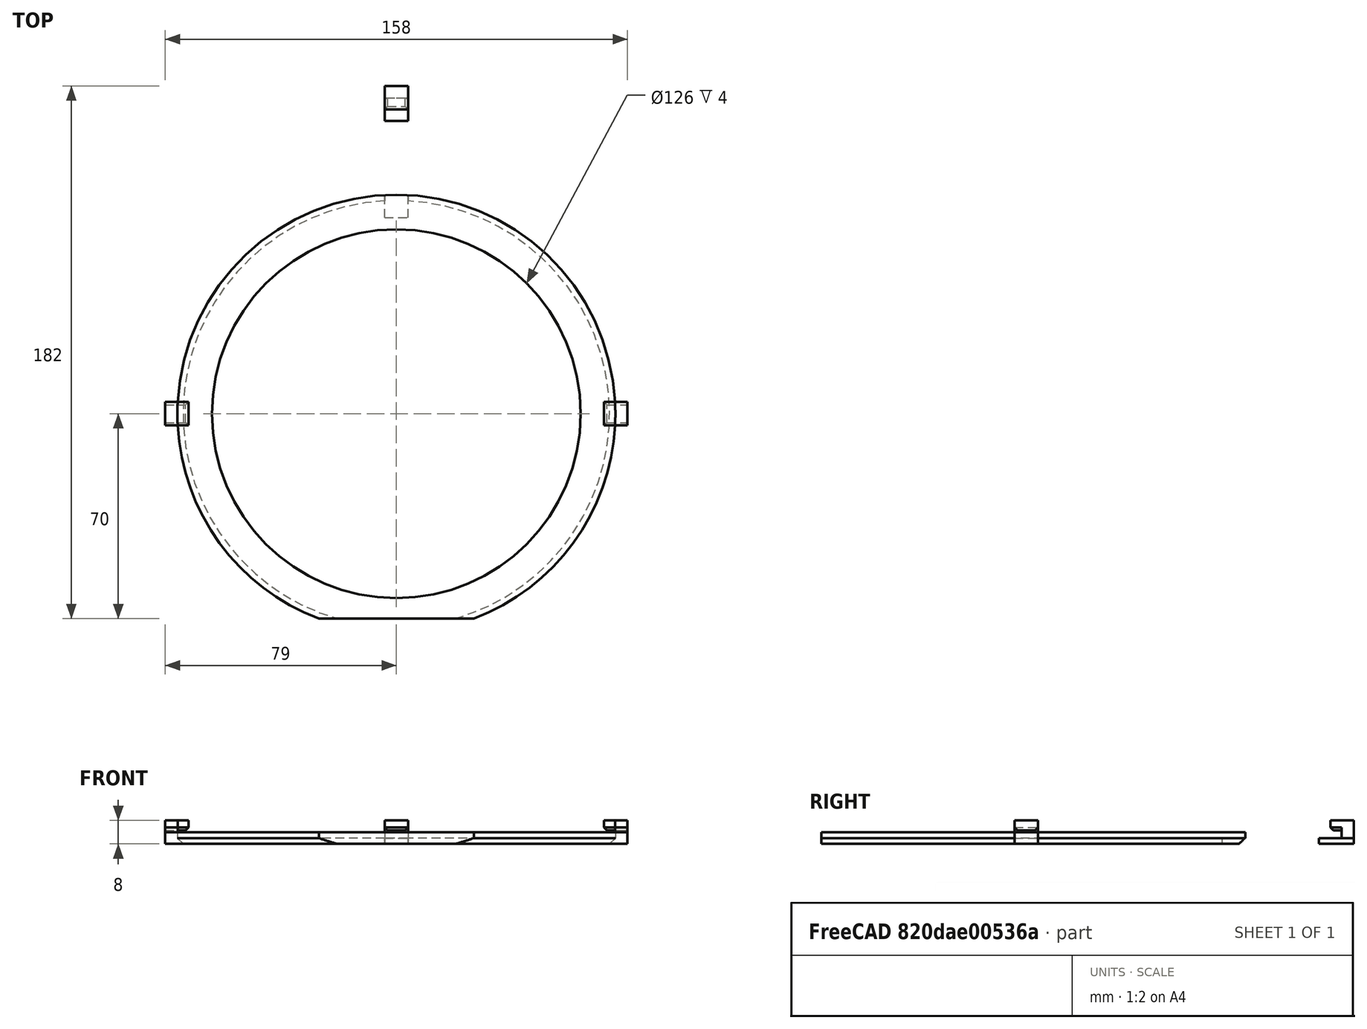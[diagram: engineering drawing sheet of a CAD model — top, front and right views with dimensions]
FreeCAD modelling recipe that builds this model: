
FCSTD DOCUMENT  (FreeCAD 0.19R0.19.2)
Label: waferHolder_007
License: All rights reserved
LicenseURL: http://en.wikipedia.org/wiki/All_rights_reserved
objects: Part::Box×15, Part::Chamfer×13, Part::Cut×8, Sketcher::SketchObject×5, Part::Extrusion×5, Part::MultiFuse×2
note: 48 computed .brp shape members not serialized (recipe doc carries the construction recipe); baked Part::Feature solids carry a one-line shape summary decoded from their .brp

FEATURE [Sketcher::SketchObject] Sketch
  FullyConstrained = true
  sketch-geometry (3):
    g0: Circle CenterX=-3.1415e-12 CenterY=5.6243e-12 CenterZ=0 NormalX=0 NormalY=0 NormalZ=1 AngleXU=0 Radius=63
    g1: ArcOfCircle CenterX=-3.1415e-12 CenterY=5.6243e-12 CenterZ=0 NormalX=0 NormalY=0 NormalZ=1 AngleXU=0 Radius=74.8482 StartAngle=5.07429 EndAngle=10.6337
    g2: LineSegment StartX=-26.5 StartY=-70.0001 StartZ=0 EndX=26.5 EndY=-70.0001 EndZ=0
  constraints (6):
    c: Block(g0)
    c: Coincident(g1,g0)
    c: Block(g1)
    c: Coincident(g2,g1)
    c: Coincident(g2,g1)
    c: Horizontal(g2)
FEATURE [Part::Box] Box  label="holderBitLeft"
  AttacherType = Attacher::AttachEngine3D
  Height = 4
  Length = 8
  Placement = pos=(-79,-4,0) rot=(0,0,1;0rad)
  Width = 8
FEATURE [Part::Box] Box001  label="bitHolderTopCutout"
  AttacherType = Attacher::AttachEngine3D
  Height = 4
  Length = 8
  Placement = pos=(-4,67,-2) rot=(0,0,1;0rad)
  Width = 12
FEATURE [Part::Extrusion] Extrude  label="mainHolderRing"
  Base = -> Sketch
  Dir = (0,0,1)
  DirMode = 2
  FaceMakerClass = Part::FaceMakerBullseye
  LengthFwd = 4
  LengthRev = 0
  Solid = true
  Symmetric = false
FEATURE [Part::Box] Box002  label="holderBitRight"
  AttacherType = Attacher::AttachEngine3D
  Height = 4
  Length = 8
  Placement = pos=(71,-4,0) rot=(0,0,1;0rad)
  Width = 8
FEATURE [Part::Box] Box003  label="bitHolderTop"
  AttacherType = Attacher::AttachEngine3D
  Height = 2
  Length = 8
  Placement = pos=(-4,100,0) rot=(0,0,1;0rad)
  Width = 12
FEATURE [Part::Chamfer] Chamfer
  Base = -> Extrude
  Edges = 1 edges r=2: [Edge3]
FEATURE [Part::Cut] Cut  label="mainHolderRing001"
  Base = -> Chamfer
  Tool = -> Box001
FEATURE [Part::Box] Box004  label="holderBitLeft001"
  AttacherType = Attacher::AttachEngine3D
  Height = 4
  Length = 6
  Placement = pos=(-79,-4,0) rot=(0,0,1;0rad)
  Width = 8
FEATURE [Part::Box] Box005  label="holderBitright002"
  AttacherType = Attacher::AttachEngine3D
  Height = 4
  Length = 6
  Placement = pos=(73,-4,0) rot=(0,0,1;0rad)
  Width = 8
FEATURE [Part::MultiFuse] Fusion  label="holders"
  Shapes = -> [Box004,Box005]
FEATURE [Sketcher::SketchObject] Sketch001
  FullyConstrained = true
  sketch-geometry (3):
    g0: Circle CenterX=-3.1415e-12 CenterY=5.6243e-12 CenterZ=0 NormalX=0 NormalY=0 NormalZ=1 AngleXU=0 Radius=63
    g1: ArcOfCircle CenterX=-3.1415e-12 CenterY=5.6243e-12 CenterZ=0 NormalX=0 NormalY=0 NormalZ=1 AngleXU=0 Radius=74.8482 StartAngle=5.07429 EndAngle=10.6337
    g2: LineSegment StartX=-26.5 StartY=-70.0001 StartZ=0 EndX=26.5 EndY=-70.0001 EndZ=0
  constraints (6):
    c: Block(g0)
    c: Coincident(g1,g0)
    c: Block(g1)
    c: Coincident(g2,g1)
    c: Coincident(g2,g1)
    c: Horizontal(g2)
FEATURE [Part::Extrusion] Extrude001  label="mainHolderRing002"
  Base = -> Sketch001
  Dir = (0,0,1)
  DirMode = 2
  FaceMakerClass = Part::FaceMakerBullseye
  LengthFwd = 4
  LengthRev = 0
  Solid = true
  Symmetric = false
FEATURE [Part::Cut] Cut001
  Base = -> Fusion
  Placement = pos=(0,0,4) rot=(0,0,1;0rad)
  Tool = -> Extrude001
FEATURE [Part::Box] Box006  label="holderBitLeft002"
  AttacherType = Attacher::AttachEngine3D
  Height = 3.4
  Length = 8
  Placement = pos=(-79,-4,4.6) rot=(0,0,1;0rad)
  Width = 8
FEATURE [Part::Box] Box007  label="holderBitRight002"
  AttacherType = Attacher::AttachEngine3D
  Height = 3.4
  Length = 8
  Placement = pos=(71,-4,4.6) rot=(0,0,1;0rad)
  Width = 8
FEATURE [Part::Box] Box008  label="holderBitLeft003"
  AttacherType = Attacher::AttachEngine3D
  Height = 2
  Length = 8
  Placement = pos=(-4,71,2) rot=(0,0,1;0rad)
  Width = 8
FEATURE [Part::Box] Box009  label="bitHolderTopCutout001"
  AttacherType = Attacher::AttachEngine3D
  Height = 4
  Length = 8
  Placement = pos=(-4,67,-2) rot=(0,0,1;0rad)
  Width = 12
FEATURE [Sketcher::SketchObject] Sketch002
  FullyConstrained = true
  sketch-geometry (3):
    g0: Circle CenterX=-3.1415e-12 CenterY=5.6243e-12 CenterZ=0 NormalX=0 NormalY=0 NormalZ=1 AngleXU=0 Radius=63
    g1: ArcOfCircle CenterX=-3.1415e-12 CenterY=5.6243e-12 CenterZ=0 NormalX=0 NormalY=0 NormalZ=1 AngleXU=0 Radius=74.8482 StartAngle=5.07429 EndAngle=10.6337
    g2: LineSegment StartX=-26.5 StartY=-70.0001 StartZ=0 EndX=26.5 EndY=-70.0001 EndZ=0
  constraints (6):
    c: Block(g0)
    c: Coincident(g1,g0)
    c: Block(g1)
    c: Coincident(g2,g1)
    c: Coincident(g2,g1)
    c: Horizontal(g2)
FEATURE [Part::Extrusion] Extrude002  label="mainHolderRing003"
  Base = -> Sketch002
  Dir = (0,0,1)
  DirMode = 2
  FaceMakerClass = Part::FaceMakerBullseye
  LengthFwd = 4
  LengthRev = 0
  Solid = true
  Symmetric = false
FEATURE [Part::Chamfer] Chamfer001
  Base = -> Extrude002
  Edges = 1 edges r=2: [Edge3]
FEATURE [Part::Cut] Cut002  label="mainHolderRing004"
  Base = -> Chamfer001
  Tool = -> Box009
FEATURE [Part::Cut] Cut003  label="bitHolderTop001"
  Base = -> Box008
  Tool = -> Cut002
FEATURE [Part::Box] Box010  label="holderBitLeft004"
  AttacherType = Attacher::AttachEngine3D
  Height = 2
  Length = 8
  Placement = pos=(-4,71,2) rot=(0,0,1;0rad)
  Width = 8
FEATURE [Part::Box] Box011  label="bitHolderTopCutout002"
  AttacherType = Attacher::AttachEngine3D
  Height = 4
  Length = 8
  Placement = pos=(-4,67,-2) rot=(0,0,1;0rad)
  Width = 12
FEATURE [Sketcher::SketchObject] Sketch003
  FullyConstrained = true
  sketch-geometry (3):
    g0: Circle CenterX=-3.1415e-12 CenterY=5.6243e-12 CenterZ=0 NormalX=0 NormalY=0 NormalZ=1 AngleXU=0 Radius=63
    g1: ArcOfCircle CenterX=-3.1415e-12 CenterY=5.6243e-12 CenterZ=0 NormalX=0 NormalY=0 NormalZ=1 AngleXU=0 Radius=74.8482 StartAngle=5.07429 EndAngle=10.6337
    g2: LineSegment StartX=-26.5 StartY=-70.0001 StartZ=0 EndX=26.5 EndY=-70.0001 EndZ=0
  constraints (6):
    c: Block(g0)
    c: Coincident(g1,g0)
    c: Block(g1)
    c: Coincident(g2,g1)
    c: Coincident(g2,g1)
    c: Horizontal(g2)
FEATURE [Part::Extrusion] Extrude003  label="mainHolderRing006"
  Base = -> Sketch003
  Dir = (0,0,1)
  DirMode = 2
  FaceMakerClass = Part::FaceMakerBullseye
  LengthFwd = 4
  LengthRev = 0
  Solid = true
  Symmetric = false
FEATURE [Part::Chamfer] Chamfer002
  Base = -> Extrude003
  Edges = 1 edges r=2: [Edge3]
FEATURE [Part::Cut] Cut005  label="mainHolderRing005"
  Base = -> Chamfer002
  Tool = -> Box011
FEATURE [Part::Cut] Cut004  label="bitHolderTop002"
  Base = -> Box010
  Placement = pos=(0,0,2) rot=(0,0,1;0rad)
  Tool = -> Cut005
FEATURE [Part::Box] Box012  label="holderBitLeft005"
  AttacherType = Attacher::AttachEngine3D
  Height = 2
  Length = 8
  Placement = pos=(-4,71,2) rot=(0,0,1;0rad)
  Width = 8
FEATURE [Part::Box] Box013  label="bitHolderTopCutout003"
  AttacherType = Attacher::AttachEngine3D
  Height = 4
  Length = 8
  Placement = pos=(-4,67,-2) rot=(0,0,1;0rad)
  Width = 12
FEATURE [Sketcher::SketchObject] Sketch004
  FullyConstrained = true
  sketch-geometry (3):
    g0: Circle CenterX=-3.1415e-12 CenterY=5.6243e-12 CenterZ=0 NormalX=0 NormalY=0 NormalZ=1 AngleXU=0 Radius=63
    g1: ArcOfCircle CenterX=-3.1415e-12 CenterY=5.6243e-12 CenterZ=0 NormalX=0 NormalY=0 NormalZ=1 AngleXU=0 Radius=74.8482 StartAngle=5.07429 EndAngle=10.6337
    g2: LineSegment StartX=-26.5 StartY=-70.0001 StartZ=0 EndX=26.5 EndY=-70.0001 EndZ=0
  constraints (6):
    c: Block(g0)
    c: Coincident(g1,g0)
    c: Block(g1)
    c: Coincident(g2,g1)
    c: Coincident(g2,g1)
    c: Horizontal(g2)
FEATURE [Part::Extrusion] Extrude004  label="mainHolderRing008"
  Base = -> Sketch004
  Dir = (0,0,1)
  DirMode = 2
  FaceMakerClass = Part::FaceMakerBullseye
  LengthFwd = 4
  LengthRev = 0
  Solid = true
  Symmetric = false
FEATURE [Part::Chamfer] Chamfer003
  Base = -> Extrude004
  Edges = 1 edges r=2: [Edge3]
FEATURE [Part::Cut] Cut007  label="mainHolderRing007"
  Base = -> Chamfer003
  Tool = -> Box013
FEATURE [Part::Cut] Cut006  label="bitHolderTop003"
  Base = -> Box012
  Placement = pos=(0,0,4) rot=(0,0,1;0rad)
  Tool = -> Cut007
FEATURE [Part::Box] Box014  label="bitHoldertop006"
  AttacherType = Attacher::AttachEngine3D
  Height = 3.4
  Length = 8
  Placement = pos=(-4,71,4.6) rot=(0,0,1;0rad)
  Width = 8
FEATURE [Part::MultiFuse] Fusion001  label="holderTop"
  Placement = pos=(0,33,0) rot=(0,0,1;0rad)
  Shapes = -> [Cut003,Cut004,Cut006,Box014]
FEATURE [Part::Chamfer] Chamfer004
  Base = -> Fusion001
  Edges = 1 edges r=1: [Edge16]
FEATURE [Part::Chamfer] Chamfer005
  Base = -> Box006
  Edges = 1 edges r=1: [Edge8]
FEATURE [Part::Chamfer] Chamfer006
  Base = -> Box007
  Edges = 1 edges r=1: [Edge4]
FEATURE [Part::Chamfer] Chamfer007
  Base = -> Chamfer006
  Edges = 1 edges r=1: [Edge13]
FEATURE [Part::Chamfer] Chamfer008
  Base = -> Chamfer007
  Edges = 1 edges r=1: [Edge5]
FEATURE [Part::Chamfer] Chamfer009
  Base = -> Chamfer004
  Edges = 1 edges r=1: [Edge1]
FEATURE [Part::Chamfer] Chamfer010
  Base = -> Chamfer009
  Edges = 1 edges r=1: [Edge32]
FEATURE [Part::Chamfer] Chamfer011
  Base = -> Chamfer005
  Edges = 1 edges r=1: [Edge5]
FEATURE [Part::Chamfer] Chamfer012
  Base = -> Chamfer011
  Edges = 1 edges r=1: [Edge16]
